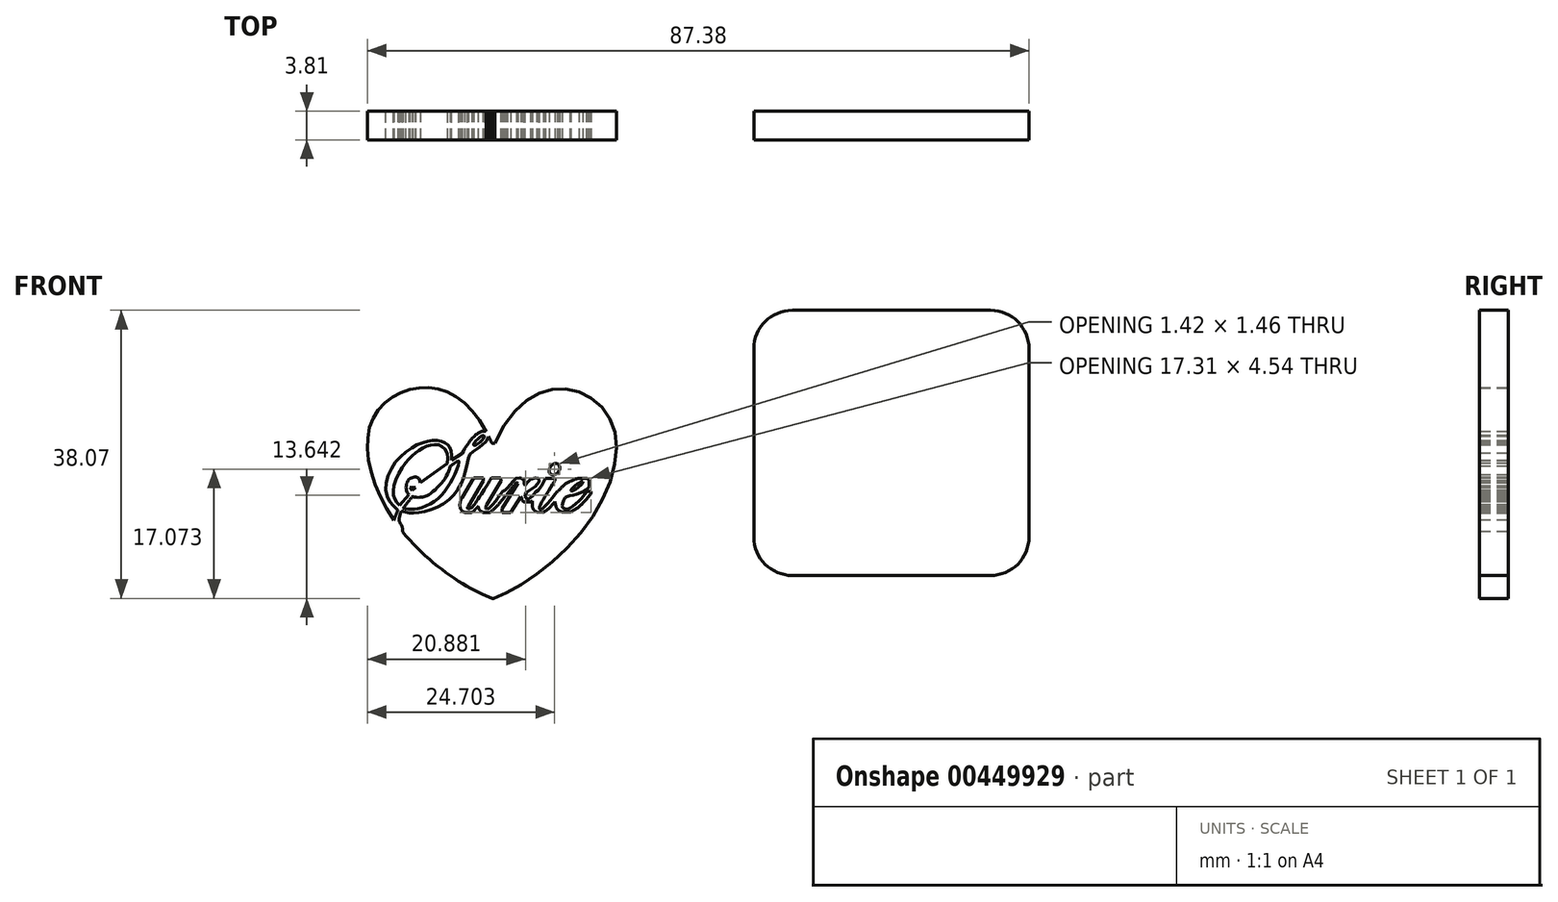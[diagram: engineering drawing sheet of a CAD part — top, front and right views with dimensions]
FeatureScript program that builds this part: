
annotation { "Feature Type Name" : "Feature", "Feature Type Description" : "" }
export const myFeature = defineFeature(function(context is Context, id is Id, definition is map)
    precondition{}
    {
        {
            var Q0;
            Q0=qCreatedBy(makeId("Front.planeOp"),FACE);
            var sketch = newSketch(context, id + "F0", { "sketchPlane" : qUnion([Q0])});
            skFitSpline(sketch, "E0", {"points": [v(-110.88, 58.7) * mm, v(-110.67, 58.71) * mm], "startDerivative": vector(0.18, 0) * mm, "endDerivative": vector(0.63, 0.01) * mm});
            skFitSpline(sketch, "E1", {"points": [v(-110.67, 58.71) * mm, v(-102.2, 65.92) * mm, v(-95.26, 61.54) * mm, v(-98.25, 48.28) * mm, v(-110.88, 38.2) * mm], "startDerivative": vector(26.18, 58.96) * mm, "endDerivative": vector(-37.48, -13.43) * mm});
            skFitSpline(sketch, "E2.MirrorCS", {"points": [v(-111.04, 58.72) * mm, v(-111.2, 58.98) * mm], "startDerivative": vector(-0.09, 0.16) * mm, "endDerivative": vector(-0.48, 0.78) * mm});
            skFitSpline(sketch, "E3.MirrorCS", {"points": [v(-111.2, 58.98) * mm, v(-119.82, 66.07) * mm, v(-126.94, 61.58) * mm, v(-123.47, 47.78) * mm, v(-110.96, 38.2) * mm], "startDerivative": vector(-25.01, 59.46) * mm, "endDerivative": vector(37.47, -13.48) * mm});
            skFitSpline(sketch, "E4", {"points": [v(-116.38, 56.46) * mm, v(-115, 57.38) * mm, v(-115, 57.37) * mm], "startDerivative": vector(2.24, 1.48) * mm, "endDerivative": vector(-0.16, -0.1) * mm});
            skFitSpline(sketch, "E5", {"points": [v(-115, 57.37) * mm, v(-112.51, 60.22) * mm, v(-111.8, 60.25) * mm], "startDerivative": vector(4.1, 7.67) * mm, "endDerivative": vector(2.06, -0.6) * mm});
            skFitSpline(sketch, "E6", {"points": [v(-111.48, 59.6) * mm, v(-113.8, 57.42) * mm, v(-114.47, 55.37) * mm, v(-116.5, 51.48) * mm, v(-120.88, 49.51) * mm, v(-123.05, 49.73) * mm], "startDerivative": vector(-5.64, -16.94) * mm, "endDerivative": vector(-12.46, 2.56) * mm});
            skFitSpline(sketch, "E7", {"points": [v(-124, 48.52) * mm, v(-123.51, 49.88) * mm], "startDerivative": vector(0.2, 1.17) * mm, "endDerivative": vector(0.2, 1.17) * mm});
            skFitSpline(sketch, "E8", {"points": [v(-123.51, 49.88) * mm, v(-124.96, 51.87) * mm, v(-124.34, 55.4) * mm, v(-121.7, 58.06) * mm, v(-119.47, 59) * mm, v(-117.93, 59.03) * mm, v(-117, 58.62) * mm, v(-116.54, 57.94) * mm, v(-116.38, 56.46) * mm], "startDerivative": vector(-13.17, 12.5) * mm, "endDerivative": vector(0.37, -15.15) * mm});
            skEllipse(sketch, "E9", {"center": v(-112.77, 59.07) * mm, "majorRadius": 0.91 * mm, "minorRadius": 0.26 * mm, "majorAxis": v(0.75, 0.66)});
            skFitSpline(sketch, "E10", {"points": [v(-116.57, 55.63) * mm, v(-117.47, 53.76) * mm, v(-119.37, 51.94) * mm, v(-120.2, 51.6) * mm, v(-121.43, 51.62) * mm, v(-121.55, 51.68) * mm], "startDerivative": vector(-2.28, -6.66) * mm, "endDerivative": vector(0.39, 0.04) * mm});
            skFitSpline(sketch, "E11", {"points": [v(-121.55, 51.68) * mm, v(-122.73, 50.21) * mm, v(-122.78, 50.14) * mm], "startDerivative": vector(-1.89, -2.26) * mm, "endDerivative": vector(-0.03, 0.06) * mm});
            skFitSpline(sketch, "E12", {"points": [v(-122.78, 50.14) * mm, v(-122.1, 50) * mm, v(-121.06, 50) * mm, v(-119.1, 50.76) * mm, v(-117.4, 52.24) * mm, v(-115.96, 54.62) * mm, v(-115.41, 56.25) * mm, v(-115.48, 56.39) * mm, v(-116.57, 55.63) * mm], "startDerivative": vector(6.9, -2.72) * mm, "endDerivative": vector(-11.37, -9.37) * mm});
            skFitSpline(sketch, "E13", {"points": [v(-123.23, 50.5) * mm, v(-122.03, 51.94) * mm, v(-122.03, 51.94) * mm], "startDerivative": vector(1.8, 2.15) * mm, "endDerivative": vector(0, 0) * mm});
            skLineSegment(sketch, "E14", {"start": v(-120.54, 53.48) * mm, "end": v(-116.99, 56.06) * mm});
            skFitSpline(sketch, "E15", {"points": [v(-116.99, 56.06) * mm, v(-116.99, 57.44) * mm, v(-117.62, 58.25) * mm, v(-118.36, 58.53) * mm, v(-119.27, 58.44) * mm, v(-120.15, 58.1) * mm, v(-121, 57.56) * mm, v(-121.81, 56.83) * mm, v(-122.85, 55.59) * mm, v(-123.89, 53.45) * mm, v(-124.06, 52.02) * mm, v(-123.82, 51.16) * mm, v(-123.23, 50.5) * mm], "startDerivative": vector(2.14, 16.2) * mm, "endDerivative": vector(9.16, -8.48) * mm});
            skFitSpline(sketch, "E16", {"points": [v(-121.09, 52.1) * mm, v(-119.96, 52.21) * mm, v(-117.88, 54.25) * mm, v(-117.48, 54.97) * mm, v(-117.43, 55.12) * mm, v(-117.43, 55.12) * mm], "startDerivative": vector(4, -0.64) * mm, "endDerivative": vector(-0.02, -0.2) * mm});
            skLineSegment(sketch, "E17", {"start": v(-121.09, 52.1) * mm, "end": v(-117.43, 55.12) * mm});
            skLineSegment(sketch, "E18", {"start": v(-121.93, 52.84) * mm, "end": v(-121.62, 52.48) * mm});
            skLineSegment(sketch, "E19", {"start": v(-121.62, 52.48) * mm, "end": v(-121.21, 52.82) * mm});
            skLineSegment(sketch, "E20", {"start": v(-121.18, 52.85) * mm, "end": v(-121.93, 52.84) * mm});
            skFitSpline(sketch, "E21", {"points": [v(-122.03, 51.94) * mm, v(-122.28, 52.32) * mm, v(-122.35, 53.28) * mm, v(-121.79, 54.1) * mm, v(-121.02, 54.23) * mm, v(-120.62, 53.94) * mm, v(-120.54, 53.48) * mm], "startDerivative": vector(-2, 2.3) * mm, "endDerivative": vector(0.12, -3.53) * mm});
            skLineSegment(sketch, "E22", {"start": v(-113.5, 54.11) * mm, "end": v(-112.17, 54.11) * mm});
            skLineSegment(sketch, "E23", {"start": v(-113.5, 54.11) * mm, "end": v(-115.02, 51.55) * mm});
            skLineSegment(sketch, "E24", {"start": v(-112.17, 54.11) * mm, "end": v(-112.17, 53.73) * mm});
            skLineSegment(sketch, "E25", {"start": v(-112.17, 53.73) * mm, "end": v(-114.2, 50.4) * mm});
            skFitSpline(sketch, "E26", {"points": [v(-115.02, 51.55) * mm, v(-115.25, 50.18) * mm], "startDerivative": vector(-0.93, -2.2) * mm, "endDerivative": vector(0.17, -1.02) * mm});
            skFitSpline(sketch, "E27", {"points": [v(-115.25, 50.18) * mm, v(-114.65, 49.58) * mm], "startDerivative": vector(0.39, -1.09) * mm, "endDerivative": vector(0.98, -0.28) * mm});
            skLineSegment(sketch, "E28", {"start": v(-114.65, 49.58) * mm, "end": v(-113.72, 49.58) * mm});
            skFitSpline(sketch, "E29", {"points": [v(-113.72, 49.58) * mm, v(-112.88, 50.36) * mm], "startDerivative": vector(1.07, 0.68) * mm, "endDerivative": vector(0.85, 0.77) * mm});
            skFitSpline(sketch, "E30", {"points": [v(-112.88, 50.37) * mm, v(-112.27, 49.58) * mm, v(-112.28, 49.58) * mm], "startDerivative": vector(0.08, -1.8) * mm, "endDerivative": vector(-0.08, 0.02) * mm});
            skLineSegment(sketch, "E31", {"start": v(-112.27, 49.58) * mm, "end": v(-111.36, 49.58) * mm});
            skFitSpline(sketch, "E32", {"points": [v(-111.36, 49.58) * mm, v(-110.35, 50.45) * mm, v(-109.2, 51.93) * mm], "startDerivative": vector(1.9, 1.19) * mm, "endDerivative": vector(2.12, 2.95) * mm});
            skLineSegment(sketch, "E33", {"start": v(-109.2, 51.93) * mm, "end": v(-109.03, 51.93) * mm});
            skFitSpline(sketch, "E34", {"points": [v(-109.03, 51.93) * mm, v(-108.44, 52.82) * mm, v(-107.8, 53.55) * mm, v(-107.8, 53.55) * mm], "startDerivative": vector(0.94, 1.62) * mm, "endDerivative": vector(0.04, -0.02) * mm});
            skLineSegment(sketch, "E35", {"start": v(-107.8, 53.55) * mm, "end": v(-107.64, 53.41) * mm});
            skLineSegment(sketch, "E36", {"start": v(-107.64, 53.41) * mm, "end": v(-109.7, 50.08) * mm});
            skLineSegment(sketch, "E37", {"start": v(-109.7, 50.08) * mm, "end": v(-109.7, 49.58) * mm});
            skLineSegment(sketch, "E38", {"start": v(-109.7, 49.58) * mm, "end": v(-108.56, 49.58) * mm});
            skLineSegment(sketch, "E39", {"start": v(-108.56, 49.58) * mm, "end": v(-107.23, 51.62) * mm});
            skLineSegment(sketch, "E40", {"start": v(-107.23, 51.62) * mm, "end": v(-107.12, 51.55) * mm});
            skFitSpline(sketch, "E41", {"points": [v(-107.12, 51.55) * mm, v(-107.03, 51.13) * mm, v(-106.76, 50.94) * mm, v(-106.76, 50.94) * mm], "startDerivative": vector(-0.05, -0.87) * mm, "endDerivative": vector(0, 0.02) * mm});
            skLineSegment(sketch, "E42", {"start": v(-106.76, 50.94) * mm, "end": v(-105.97, 50.94) * mm});
            skLineSegment(sketch, "E43", {"start": v(-105.97, 50.94) * mm, "end": v(-105.7, 51.1) * mm});
            skLineSegment(sketch, "E44", {"start": v(-105.7, 51.1) * mm, "end": v(-105.7, 50.27) * mm});
            skFitSpline(sketch, "E45", {"points": [v(-105.7, 50.27) * mm, v(-105.52, 49.9) * mm, v(-105.14, 49.62) * mm], "startDerivative": vector(0.28, -0.8) * mm, "endDerivative": vector(0.83, -0.5) * mm});
            skLineSegment(sketch, "E46", {"start": v(-105.14, 49.62) * mm, "end": v(-104.24, 49.58) * mm});
            skFitSpline(sketch, "E47", {"points": [v(-104.24, 49.58) * mm, v(-103.51, 50.15) * mm, v(-102.76, 51) * mm], "startDerivative": vector(1.56, 1.08) * mm, "endDerivative": vector(1.4, 1.73) * mm});
            skFitSpline(sketch, "E48", {"points": [v(-102.76, 51) * mm, v(-102.42, 50) * mm, v(-101.78, 49.62) * mm], "startDerivative": vector(0.42, -2.1) * mm, "endDerivative": vector(1.57, -0.62) * mm});
            skLineSegment(sketch, "E49", {"start": v(-101.78, 49.62) * mm, "end": v(-100.78, 49.6) * mm});
            skFitSpline(sketch, "E50", {"points": [v(-100.78, 49.6) * mm, v(-99.75, 50.17) * mm, v(-98.05, 51.97) * mm], "startDerivative": vector(2.47, 1.04) * mm, "endDerivative": vector(2.97, 3.55) * mm});
            skLineSegment(sketch, "E51", {"start": v(-98.05, 51.97) * mm, "end": v(-98, 52.07) * mm});
            skLineSegment(sketch, "E52", {"start": v(-98, 52.07) * mm, "end": v(-97.98, 52.36) * mm});
            skLineSegment(sketch, "E53", {"start": v(-97.98, 52.36) * mm, "end": v(-98.48, 52.36) * mm});
            skFitSpline(sketch, "E54", {"points": [v(-98.48, 52.36) * mm, v(-99.65, 50.99) * mm, v(-100.74, 50.15) * mm, v(-101.15, 49.99) * mm, v(-101.45, 50.03) * mm, v(-101.74, 50.22) * mm, v(-101.74, 50.8) * mm, v(-101.35, 51.56) * mm, v(-100.67, 51.77) * mm, v(-99.36, 52.17) * mm, v(-98.48, 52.65) * mm, v(-98.22, 53.01) * mm], "startDerivative": vector(-8.08, -10.45) * mm, "endDerivative": vector(2.28, 6.15) * mm});
            skLineSegment(sketch, "E55", {"start": v(-98.22, 53.01) * mm, "end": v(-98.22, 53.7) * mm});
            skFitSpline(sketch, "E56", {"points": [v(-98.22, 53.7) * mm, v(-98.6, 54.09) * mm], "startDerivative": vector(-0.2, 0.52) * mm, "endDerivative": vector(-0.95, 0.42) * mm});
            skLineSegment(sketch, "E57", {"start": v(-98.6, 54.09) * mm, "end": v(-99.58, 54.09) * mm});
            skFitSpline(sketch, "E58", {"points": [v(-114.2, 50.4) * mm, v(-114.26, 50.11) * mm, v(-114.08, 50.05) * mm, v(-113.66, 50.3) * mm, v(-111.13, 54.12) * mm], "startDerivative": vector(-1.03, -2.37) * mm, "endDerivative": vector(5.32, 8.77) * mm});
            skLineSegment(sketch, "E59", {"start": v(-111.13, 54.12) * mm, "end": v(-109.88, 54.12) * mm});
            skLineSegment(sketch, "E60", {"start": v(-109.88, 54.12) * mm, "end": v(-109.86, 53.76) * mm});
            skLineSegment(sketch, "E61", {"start": v(-109.86, 53.76) * mm, "end": v(-111.73, 50.56) * mm});
            skFitSpline(sketch, "E62", {"points": [v(-111.73, 50.56) * mm, v(-111.91, 50.2) * mm, v(-111.88, 50.08) * mm, v(-111.58, 50.07) * mm, v(-109.59, 52.4) * mm], "startDerivative": vector(-1.23, -2.02) * mm, "endDerivative": vector(4.33, 6.04) * mm});
            skLineSegment(sketch, "E63", {"start": v(-109.59, 52.4) * mm, "end": v(-109.37, 52.4) * mm});
            skFitSpline(sketch, "E64", {"points": [v(-109.37, 52.4) * mm, v(-109.33, 52.45) * mm, v(-108.03, 53.98) * mm, v(-107.83, 54.1) * mm, v(-107.08, 54.1) * mm, v(-106.8, 53.73) * mm, v(-106.8, 53.27) * mm, v(-106.63, 53.14) * mm, v(-106.47, 53.41) * mm, v(-105.76, 54.07) * mm, v(-104.96, 54.11) * mm, v(-104.88, 54) * mm, v(-104.9, 53.41) * mm, v(-106.22, 52.4) * mm, v(-106.5, 52.26) * mm, v(-106.65, 51.93) * mm, v(-106.65, 51.56) * mm, v(-106.38, 51.32) * mm, v(-105.73, 51.7) * mm, v(-105.17, 52.4) * mm, v(-104.95, 52.46) * mm, v(-104.03, 54.06) * mm], "startDerivative": vector(1.1, 1.4) * mm, "endDerivative": vector(11.94, 25.63) * mm});
            skLineSegment(sketch, "E65", {"start": v(-104.03, 54.06) * mm, "end": v(-102.74, 54.06) * mm});
            skLineSegment(sketch, "E66", {"start": v(-102.74, 54.06) * mm, "end": v(-102.73, 53.75) * mm});
            skFitSpline(sketch, "E67", {"points": [v(-102.73, 53.75) * mm, v(-104.55, 50.78) * mm, v(-104.75, 50.3) * mm, v(-104.78, 50.02) * mm, v(-104.52, 50) * mm, v(-102.43, 52.38) * mm], "startDerivative": vector(-6.62, -10.47) * mm, "endDerivative": vector(7.51, 9.93) * mm});
            skLineSegment(sketch, "E68", {"start": v(-102.43, 52.38) * mm, "end": v(-102.3, 52.38) * mm});
            skFitSpline(sketch, "E69", {"points": [v(-102.3, 52.38) * mm, v(-101.65, 53.08) * mm, v(-100.63, 53.74) * mm, v(-99.58, 54.09) * mm], "startDerivative": vector(1.88, 2.28) * mm, "endDerivative": vector(3.11, 0.86) * mm});
            skEllipse(sketch, "E70", {"center": v(-102.8, 55.28) * mm, "majorRadius": 0.82 * mm, "minorRadius": 0.63 * mm, "majorAxis": v(-0.64, -0.77)});
            skEllipse(sketch, "E71", {"center": v(-99.83, 53.02) * mm, "majorRadius": 0.99 * mm, "minorRadius": 0.22 * mm, "majorAxis": v(0.8, 0.61)});
            skLineSegment(sketch, "E72", {"start": v(-124.22, 48.85) * mm, "end": v(-124.22, 48.85) * mm});
            skLineSegment(sketch, "E73", {"start": v(-111.04, 58.72) * mm, "end": v(-110.88, 58.7) * mm});
            skLineSegment(sketch, "E74", {"start": v(-110.96, 38.2) * mm, "end": v(-110.88, 38.2) * mm});
            skFitSpline(sketch, "E75", {"points": [v(-123.05, 49.73) * mm, v(-123.25, 49) * mm, v(-123.26, 48.3) * mm, v(-122.92, 47.68) * mm, v(-122.88, 47.03) * mm], "startDerivative": vector(-0.9, -2.77) * mm, "endDerivative": vector(-0.18, -2.75) * mm});
            skLineSegment(sketch, "E76", {"start": v(-124, 48.52) * mm, "end": v(-122.88, 47.03) * mm});
            skLineSegment(sketch, "E77", {"start": v(-112.88, 50.37) * mm, "end": v(-112.88, 50.36) * mm});
            skLineSegment(sketch, "E78", {"start": v(-121.21, 52.82) * mm, "end": v(-121.18, 52.85) * mm});
            skLineSegment(sketch, "E79.bottom", {"start": v(-92.6, 68.7) * mm, "end": v(-129.68, 68.7) * mm});
            skLineSegment(sketch, "E79.top", {"start": v(-92.6, 36.34) * mm, "end": v(-129.68, 36.34) * mm});
            skLineSegment(sketch, "E79.left", {"start": v(-92.6, 68.7) * mm, "end": v(-92.6, 36.34) * mm});
            skLineSegment(sketch, "E79.right", {"start": v(-129.68, 68.7) * mm, "end": v(-129.68, 36.34) * mm});
            skSolve(sketch);
        }
        {
            var Q0;
            Q0=makeQuery(id+"F0.imprint","IMPRINT",FACE,{"disambiguationData":[TD([[makeQuery(id+"F0.imprint","IMPRINT",EDGE,{"derivedFrom":sQuery(id+"F0.wireOp",EDGE,"E0")}),-1.0]])]});
            var Q1;
            {var subQ5=sQuery(id+"F0.wireOp",EDGE,"E7");Q1=makeQuery(id+"F0.imprint","IMPRINT",FACE,{"disambiguationData":[TD([[makeQuery(id+"F0.imprint","IMPRINT",EDGE,{"derivedFrom":subQ5}),1.0]])]});}
            var Q2;
            Q2=makeQuery(id+"F0.imprint","IMPRINT",FACE,{"disambiguationData":[TD([[makeQuery(id+"F0.imprint","IMPRINT",EDGE,{"derivedFrom":sQuery(id+"F0.wireOp",EDGE,"E13")}),1.0]])]});
            var Q3;
            {var subQ0=sQuery(id+"F0.wireOp",EDGE,"E12");var subQ1=sQuery(id+"F0.wireOp",EDGE,"E10");var subQ2=makeQuery(id+"F0.imprint","INTERSECT",VERTEX,{"derivedFrom":[subQ1,subQ0]});Q3=makeQuery(id+"F0.imprint","IMPRINT",FACE,{"disambiguationData":[TD([[makeQuery(id+"F0.imprint","IMPRINT",EDGE,{"disambiguationData":[TD([[subQ2,-1.0]])],"derivedFrom":subQ1}),1.0]])]});}
            var Q4;
            {var subQ0=sQuery(id+"F0.wireOp",EDGE,"E17");var subQ1=sQuery(id+"F0.wireOp",EDGE,"E16");var subQ2=makeQuery(id+"F0.imprint","INTERSECT",VERTEX,{"disambiguationData":[OD(0.0)],"derivedFrom":[subQ1,subQ0]});Q4=makeQuery(id+"F0.imprint","IMPRINT",FACE,{"disambiguationData":[TD([[makeQuery(id+"F0.imprint","IMPRINT",EDGE,{"disambiguationData":[TD([[subQ2,-1.0]])],"derivedFrom":subQ1}),1.0]])]});}
            var Q5;
            Q5=makeQuery(id+"F0.imprint","IMPRINT",FACE,{"disambiguationData":[TD([[makeQuery(id+"F0.imprint","IMPRINT",EDGE,{"derivedFrom":sQuery(id+"F0.wireOp",EDGE,"E18")}),1.0]])]});
            var Q6;
            Q6=makeQuery(id+"F0.imprint","IMPRINT",FACE,{"disambiguationData":[TD([[makeQuery(id+"F0.imprint","IMPRINT",EDGE,{"derivedFrom":sQuery(id+"F0.wireOp",EDGE,"E9")}),1.0]])]});
            var Q7;
            Q7=makeQuery(id+"F0.imprint","IMPRINT",FACE,{"disambiguationData":[TD([[makeQuery(id+"F0.imprint","IMPRINT",EDGE,{"derivedFrom":sQuery(id+"F0.wireOp",EDGE,"E71")}),1.0]])]});
            extrude(context, id + "F1", {"entities" : qUnion([Q0, Q1, Q2, Q3, Q4, Q5, Q6, Q7]), "oppositeDirection" : true, "depth" : 3.8 * mm});
        }
        {
            var Q0;
            Q0=qCreatedBy(makeId("Front.planeOp"),FACE);
            var sketch = newSketch(context, id + "F2", { "sketchPlane" : qUnion([Q0])});
            skLineSegment(sketch, "E80.bottom", {"start": v(-76.47, 76.28) * mm, "end": v(-40.13, 76.28) * mm});
            skLineSegment(sketch, "E80.top", {"start": v(-76.47, 41.24) * mm, "end": v(-40.13, 41.24) * mm});
            skLineSegment(sketch, "E80.left", {"start": v(-76.47, 76.28) * mm, "end": v(-76.47, 41.24) * mm});
            skLineSegment(sketch, "E80.right", {"start": v(-40.13, 76.28) * mm, "end": v(-40.13, 41.24) * mm});
            skSolve(sketch);
        }
        {
            var Q0;
            Q0=makeQuery(id+"F2.imprint","IMPRINT",FACE,{"disambiguationData":[TD([[makeQuery(id+"F2.imprint","IMPRINT",EDGE,{"derivedFrom":sQuery(id+"F2.wireOp",EDGE,"E80.bottom")}),-1.0]])]});
            extrude(context, id + "F3", {"entities" : qUnion([Q0]), "oppositeDirection" : true, "depth" : 3.8 * mm});
        }
        {
            var Q0;
            Q0=makeQuery(id+"F3.opExtrude","SWEPT_EDGE",EDGE,{"disambiguationData":[OSD([sQuery(id+"F2.wireOp",EDGE,"E80.bottom"),sQuery(id+"F2.wireOp",EDGE,"E80.right")])]});
            var Q1;
            Q1=makeQuery(id+"F3.opExtrude","SWEPT_EDGE",EDGE,{"disambiguationData":[OSD([sQuery(id+"F2.wireOp",EDGE,"E80.top"),sQuery(id+"F2.wireOp",EDGE,"E80.right")])]});
            var Q2;
            Q2=makeQuery(id+"F3.opExtrude","SWEPT_EDGE",EDGE,{"disambiguationData":[OSD([sQuery(id+"F2.wireOp",EDGE,"E80.bottom"),sQuery(id+"F2.wireOp",EDGE,"E80.left")])]});
            var Q3;
            Q3=makeQuery(id+"F3.opExtrude","SWEPT_EDGE",EDGE,{"disambiguationData":[OSD([sQuery(id+"F2.wireOp",EDGE,"E80.top"),sQuery(id+"F2.wireOp",EDGE,"E80.left")])]});
            fillet(context, id + "F4", {"entities" : qUnion([Q0, Q1, Q2, Q3]), "radius" : 5.08 * mm, "tangentPropagation" : true, "allowEdgeOverflow" : false});
        }
    });
